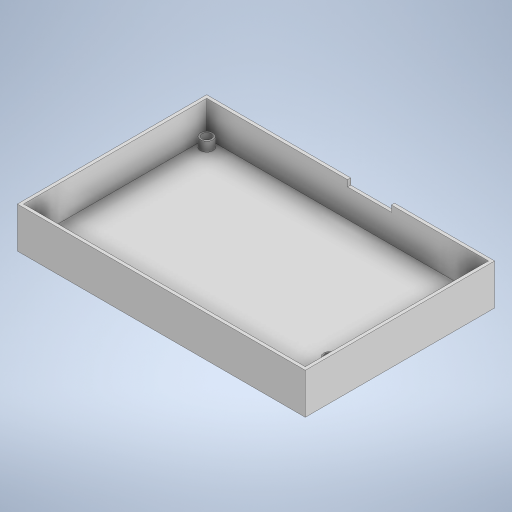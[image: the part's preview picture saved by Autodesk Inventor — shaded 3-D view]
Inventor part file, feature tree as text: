
AUTODESK INVENTOR PART (.ipt)
format: ipt  version: 2023 (Build 270158000, 158)  size: 633,856 bytes
history: native  units: mm
features: extrude x4, sketch x3, other x1, imported_body x1
ambient origin geometry x8: Origin, YZ Plane, XZ Plane, XY Plane, X Axis, Y Axis, Z Axis, Center Point
bodies: Body1 (feature_tree)
feature tree (9):
  other  "Sólido1"
  extrude  "Base - Estrutura"  Depth=121.0mm
  extrude  "Base Interna"  Depth=180.0mm
  extrude  "Furos do Pino Guia"  Depth=22.0mm TaperAngle=0.0deg
  extrude  "Chaveta para USB-C ESP32"  Depth=6.0mm
  imported_body  "Base"
  sketch  "Esboço2"  dims[d0=184.0mm d1=121.0mm]
  sketch  "Esboço3"  dims[d2=26.0mm d3=0.0mm d4=180.0mm]
  sketch  "Esboço4"  dims[d5=117.0mm d6=22.0mm d7=0.0mm d8=8.0mm d9=7.0mm d10=7.0mm d11=6.0mm d12=7.0mm d13=7.0mm d14=8.0mm d15=31.51mm d16=15.73mm d17=6.0mm d18=6.0mm d19=0.0mm d20=120.0mm d21=28.0mm d22=0.0mm d24=4.0mm d25=4.0mm d26=2.0mm d27=0.0mm d28=0.0mm d29=6.0mm d30=8.0mm d31=8.0mm d32=6.0mm]
